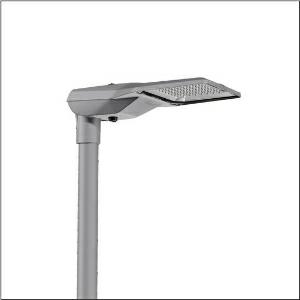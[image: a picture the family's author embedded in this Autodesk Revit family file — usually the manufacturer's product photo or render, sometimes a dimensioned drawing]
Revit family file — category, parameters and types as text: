
# Revit family: streetlight_sl_21_midi___st0_8a_5xe3c43t08mb_e12c
name_source: partatom
category: Lighting Fixtures
units: mm (PartAtom-declared; Revit-internal decimal feet)

## family parameters
Cut with Voids When Loaded = No
Host = Face
Light Source = No
Part Type = Normal
Room Calculation Point = No
Round Connector Dimension = Use Diameter
Shared = No

## types (1)
- --- (1 x LED, 20180 lm, 147 W, 4000K)
    Apparent Load = 147 VA
    CIE Flux Codes = 38 75 97 100 100
    Color Rendering = 70
    Color Temperature = 4000K
    Default Elevation = 1800 mm
    Description = Streetlight SL 21 midi, mast luminaire, primary light control with lens, of PMMA, primary optical cover: cover, of toughened safety glass, transparent, light distribution: ST0.8a, light emission: direct distribution, primary light characteristic: asymmetric, installation type: side-entry, post-top, LED, High Power LED, rated luminous flux: 20.180lm, luminous efficacy: 137lm/W, light colour: 740, colour temperature: 4000K, control gear: D4i, control: overheat protection, constant luminous flux control, time-dependent luminous flux control, flexible luminous flux parameterisation, pre-setting: logarithmic dimming characteristic, mains connection: 230..240V, AC, 50/60Hz, start of lifetime: 147W, end of service life: 155W, reduction: 65W, luminaire housing, of diecast aluminium, powder-coated, SITECO metallic grey (DB 702S), corrosivity category C5 high according to DIN EN ISO 12944, please order mast flange separately, inclination adjustable: 0°, 5°, 10°, 15°, sealing non-destructively replaceable, multi-level sealing system, length: 644mm, width: 335mm, height: 110mm, mast flange for spigot size: 42mm (side-entry): 5XC10008XM4, 60/48mm (side-entry/post-top): 5XC10108XM2, 76/60mm (side-entry/post-top): 5XC10108XM1, mounting height: 4..8m, Smart Interface below and above, protection rating (complete): IP66, insulation class (complete): insulation class II (safety insulation), certification: CE, ENEC, ENEC+, VDE, impact resistance: IK10, permissible operating ambient temperature for outdoor applications: -40..+50°C, standard-compliant lighting for roads and squares, packaging unit: 1 piece

Light Distribution: ST0.8a
    Height = 111 mm
    Lamp = 1 x LED
    Lamp Light Flux = 20180 lm
    Lamp Power = 147 W
    Lamp count = 1
    Length = 644 mm
    Luminous efficacy = 137 lm/W
    Manufacturer = Siteco
    ModVariant = No
    Model = 5XE3C43T08MB
    Number of Poles = 1
    OnlyDefault = Yes
    Power Factor = 1
    Product Name = Streetlight SL 21 midi | ST0.8a
    Product group = mast luminaire | pylon top
    ProductGroupID = 6100
    Protection Class = Protection class II
    Protection Degree = IP 66
    RLX_Detail_Level = 1
    RLX_Emergency_Light_Flux = 0 lm
    RLX_Emergency_Type = 0
    RLX_Emergency_Type_DB = No
    RlxData = <blob elided: 27093 chars, md5=09b0cadc>
    Socket = socket
    Standby Power = 0 W
    System Light Flux = 20180 lm
    System Power = 147 W
    Type Comments = factory setting: luminous flux: 100 % | dim-lin: 254 | 750 mA
    Type Image = l_1004304.jpg
    URL = http://relux.com
    VarID = @adj_183455
    Voltage = 0 V
    Weight = 0.00 kg
    Width = 336 mm

## geometry (parser evidence)
native form markers: Blend x4, Sweep x12
no freeform markers — native parametric forms only
